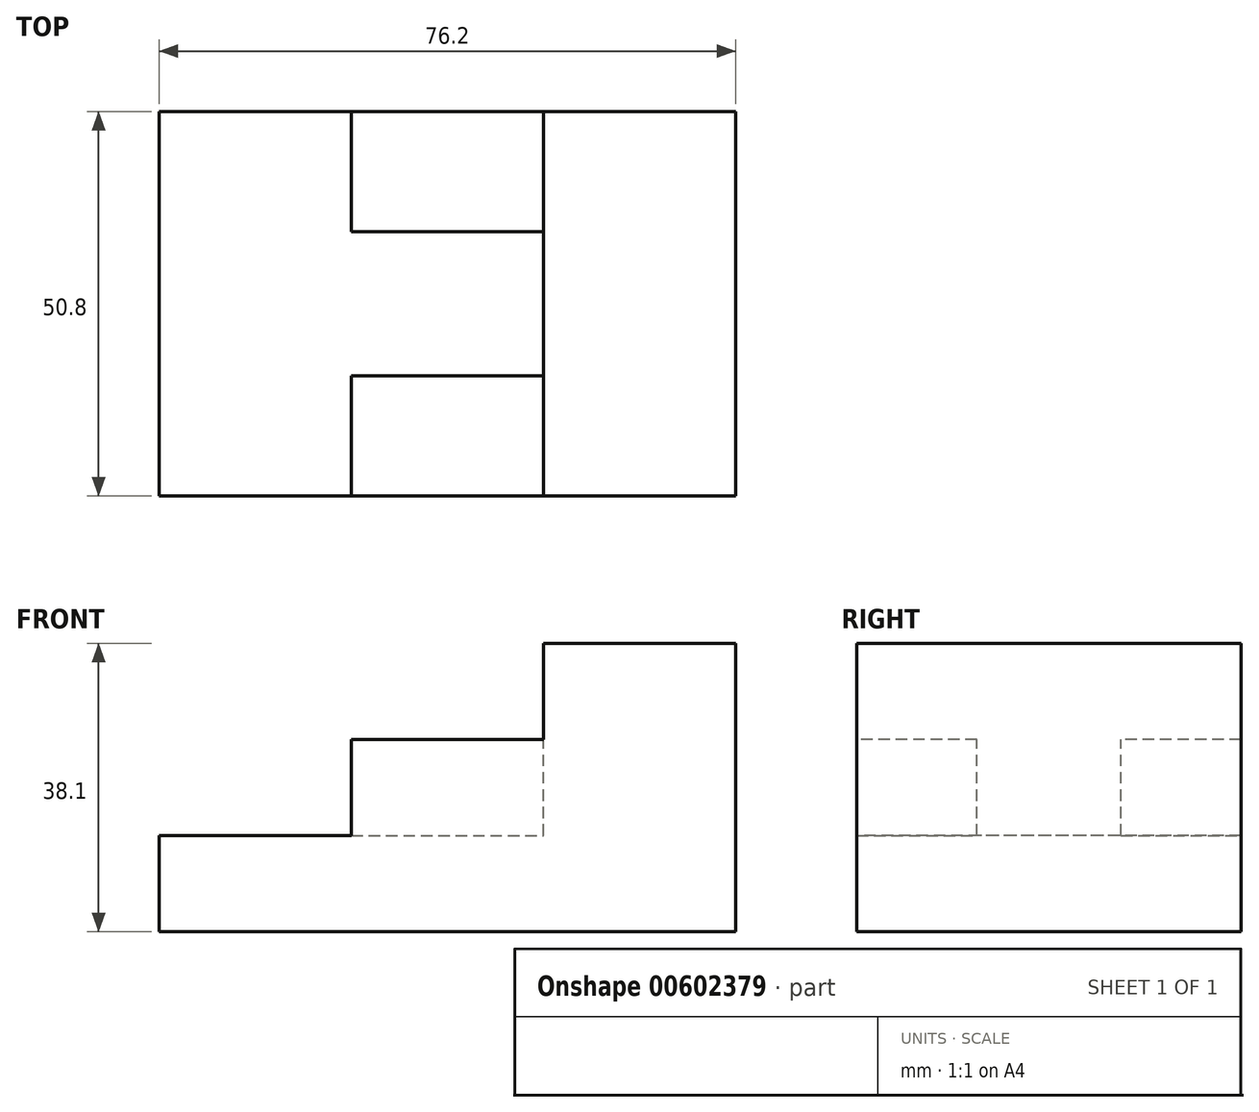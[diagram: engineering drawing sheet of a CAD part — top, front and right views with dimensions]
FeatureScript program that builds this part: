
annotation { "Feature Type Name" : "Feature", "Feature Type Description" : "" }
export const myFeature = defineFeature(function(context is Context, id is Id, definition is map)
    precondition{}
    {
        {
            var Q0;
            Q0=qCreatedBy(makeId("Top.planeOp"),FACE);
            var sketch = newSketch(context, id + "F0", { "sketchPlane" : qUnion([Q0])});
            skLineSegment(sketch, "E0.bottom", {"start": v(38.1, 25.4) * mm, "end": v(-38.1, 25.4) * mm});
            skLineSegment(sketch, "E0.top", {"start": v(38.1, -25.4) * mm, "end": v(-38.1, -25.4) * mm});
            skLineSegment(sketch, "E0.left", {"start": v(38.1, 25.4) * mm, "end": v(38.1, -25.4) * mm});
            skLineSegment(sketch, "E0.right", {"start": v(-38.1, 25.4) * mm, "end": v(-38.1, -25.4) * mm});
            skPoint(sketch, "E0.middle", {"position": v(0, 0) * mm});
            skSolve(sketch);
        }
        {
            var Q0;
            Q0 = qSketchRegion(id + "F0", true);
            extrude(context, id + "F1", {"entities" : qUnion([Q0]), "depth" : 12.7 * mm, "offsetDistance" : 25.4 * mm});
        }
        {
            var Q0;
            Q0=makeQuery(id+"F1.opExtrude","CAP_FACE",FACE,{"disambiguationData":[OSD([sQuery(id+"F0.wireOp",EDGE,"E0.bottom"),sQuery(id+"F0.wireOp",EDGE,"E0.top"),sQuery(id+"F0.wireOp",EDGE,"E0.left"),sQuery(id+"F0.wireOp",EDGE,"E0.right")])],"isStart":false});
            var sketch = newSketch(context, id + "F2", { "sketchPlane" : qUnion([Q0])});
            skLineSegment(sketch, "E1.bottom", {"start": v(38.1, -25.4) * mm, "end": v(-12.7, -25.4) * mm});
            skLineSegment(sketch, "E1.top", {"start": v(38.1, 25.4) * mm, "end": v(-12.7, 25.4) * mm});
            skLineSegment(sketch, "E1.left", {"start": v(38.1, -25.4) * mm, "end": v(38.1, 25.4) * mm});
            skLineSegment(sketch, "E1.right", {"start": v(-12.7, -25.4) * mm, "end": v(-12.7, 25.4) * mm});
            skSolve(sketch);
        }
        {
            var Q0;
            Q0 = qSketchRegion(id + "F2", true);
            extrude(context, id + "F3", {"entities" : qUnion([Q0]), "operationType" : NewBodyOperationType.ADD, "depth" : 12.7 * mm, "offsetDistance" : 25.4 * mm});
        }
        {
            var Q0;
            Q0=makeQuery(id+"F3.opExtrude","CAP_FACE",FACE,{"disambiguationData":[OSD([sQuery(id+"F2.wireOp",EDGE,"E1.bottom"),sQuery(id+"F2.wireOp",EDGE,"E1.top"),sQuery(id+"F2.wireOp",EDGE,"E1.left"),sQuery(id+"F2.wireOp",EDGE,"E1.right")])],"isStart":false});
            var sketch = newSketch(context, id + "F4", { "sketchPlane" : qUnion([Q0])});
            skLineSegment(sketch, "E2.bottom", {"start": v(-12.7, 9.52) * mm, "end": v(12.7, 9.52) * mm});
            skLineSegment(sketch, "E2.top", {"start": v(-12.7, -9.53) * mm, "end": v(12.7, -9.53) * mm});
            skLineSegment(sketch, "E2.left", {"start": v(-12.7, 9.52) * mm, "end": v(-12.7, -9.53) * mm});
            skLineSegment(sketch, "E2.right", {"start": v(12.7, 9.52) * mm, "end": v(12.7, -9.53) * mm});
            skPoint(sketch, "E2.middle", {"position": v(0, 0) * mm});
            skSolve(sketch);
        }
        {
            var Q0;
            Q0 = qSketchRegion(id + "F4", true);
            extrude(context, id + "F5", {"entities" : qUnion([Q0]), "operationType" : NewBodyOperationType.REMOVE, "oppositeDirection" : true, "depth" : 12.7 * mm, "offsetDistance" : 25.4 * mm});
        }
        {
            var Q0;
            Q0=makeQuery(id+"F3.opExtrude","CAP_FACE",FACE,{"disambiguationData":[OSD([sQuery(id+"F2.wireOp",EDGE,"E1.bottom"),sQuery(id+"F2.wireOp",EDGE,"E1.top"),sQuery(id+"F2.wireOp",EDGE,"E1.left"),sQuery(id+"F2.wireOp",EDGE,"E1.right")])],"isStart":false});
            var sketch = newSketch(context, id + "F6", { "sketchPlane" : qUnion([Q0])});
            skLineSegment(sketch, "E3.bottom", {"start": v(38.1, 25.4) * mm, "end": v(12.7, 25.4) * mm});
            skLineSegment(sketch, "E3.top", {"start": v(38.1, -25.4) * mm, "end": v(12.7, -25.4) * mm});
            skLineSegment(sketch, "E3.left", {"start": v(38.1, 25.4) * mm, "end": v(38.1, -25.4) * mm});
            skLineSegment(sketch, "E3.right", {"start": v(12.7, 25.4) * mm, "end": v(12.7, -25.4) * mm});
            skSolve(sketch);
        }
        {
            var Q0;
            Q0 = qSketchRegion(id + "F6", true);
            var Q1;
            {var subQ2=sQuery(id+"F6.wireOp",EDGE,"E3.bottom");Q1=makeQuery(id+"F6.imprint","IMPRINT",FACE,{"disambiguationData":[TD([[makeQuery(id+"F6.imprint","IMPRINT",EDGE,{"derivedFrom":subQ2}),1.0]])]});}
            extrude(context, id + "F7", {"entities" : qUnion([Q0, Q1]), "operationType" : NewBodyOperationType.ADD, "depth" : 12.7 * mm, "offsetDistance" : 25.4 * mm});
        }
    });
